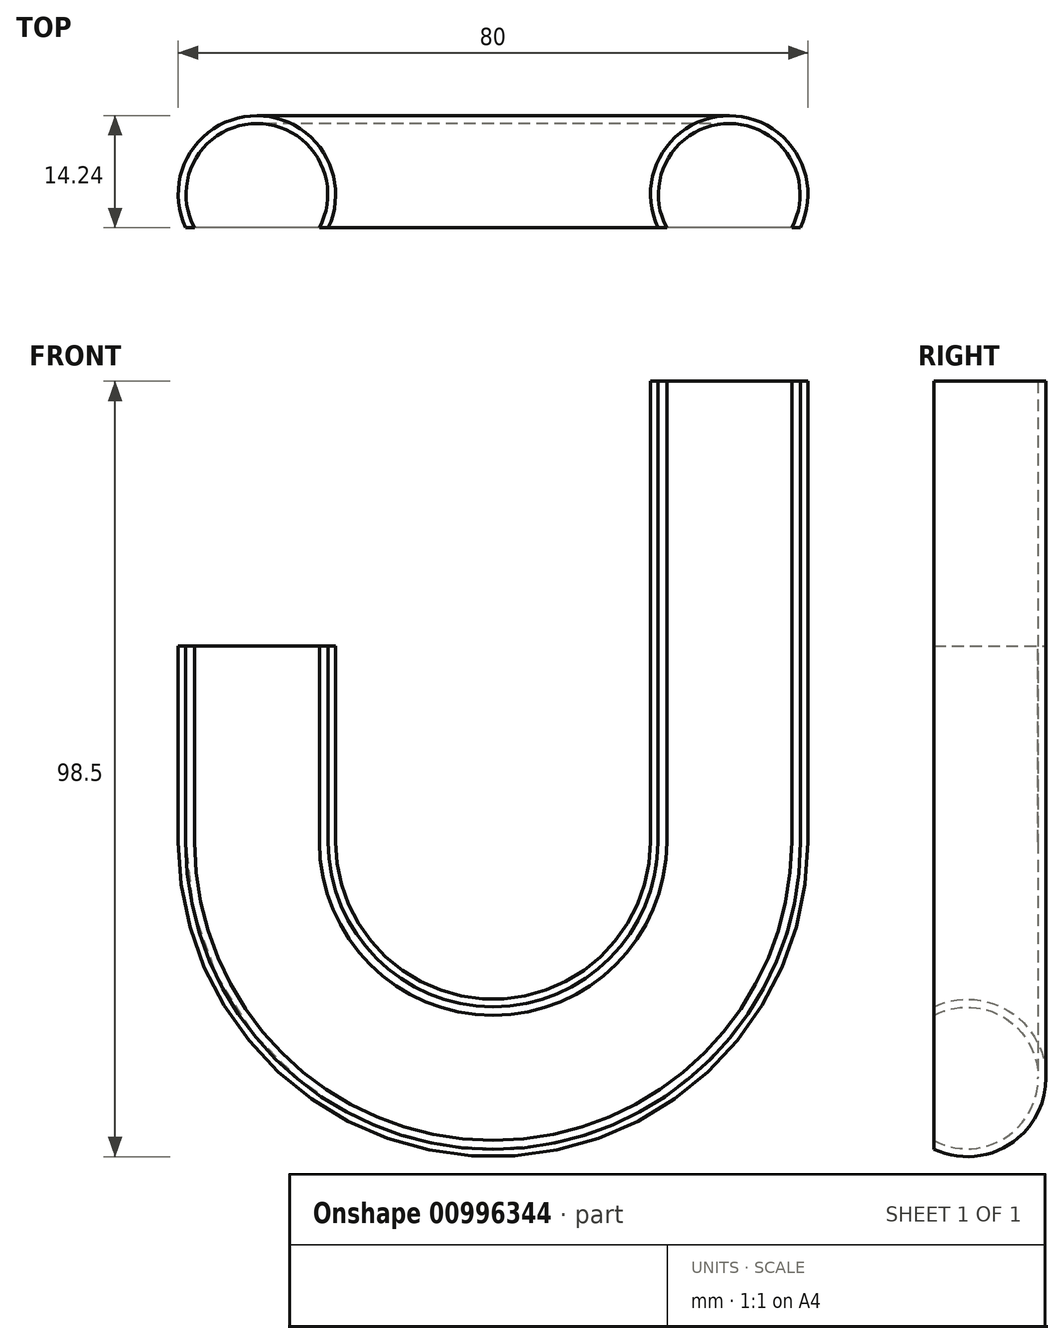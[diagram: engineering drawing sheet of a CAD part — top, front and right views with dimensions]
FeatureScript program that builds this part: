
annotation { "Feature Type Name" : "Feature", "Feature Type Description" : "" }
export const myFeature = defineFeature(function(context is Context, id is Id, definition is map)
    precondition{}
    {
        {
            var Q0;
            Q0=qCreatedBy(makeId("Front.planeOp"),FACE);
            var sketch = newSketch(context, id + "F0", { "sketchPlane" : qUnion([Q0])});
            skLineSegment(sketch, "E0", {"start": v(-30, 24.9) * mm, "end": v(-30, 0) * mm});
            skLineSegment(sketch, "E1", {"start": v(30, 58.5) * mm, "end": v(30, 0) * mm});
            skArc(sketch, "E2", {"start": v(-30, 0) * mm, "mid": v(0, -30) * mm, "end": v(30, 0) * mm});
            skSolve(sketch);
        }
        {
            var Q0;
            Q0=sQuery(id+"F0.wireOp",VERTEX,"E1.start");
            var Q1;
            Q1=sQuery(id+"F0.wireOp",EDGE,"E1");
            cPlane(context, id + "F1", {"entities" : qUnion([Q0, Q1]), "cplaneType" : CPlaneType.CURVE_POINT, "offset" : 25 * mm, "width" : 150 * mm, "height" : 150 * mm});
        }
        {
            var Q0;
            Q0=qCreatedBy(id+"F1.planeOp",FACE);
            var sketch = newSketch(context, id + "F2", { "sketchPlane" : qUnion([Q0])});
            skCircle(sketch, "E3", {"center": v(30, 0) * mm, "radius": 10 * mm});
            skSolve(sketch);
        }
        {
            var Q0;
            Q0=makeQuery(id+"F2.imprint","IMPRINT",FACE,{"disambiguationData":[TD([[makeQuery(id+"F2.imprint","IMPRINT",EDGE,{"derivedFrom":sQuery(id+"F2.wireOp",EDGE,"E3")}),1.0]])]});
            var Q1;
            Q1=sQuery(id+"F0.wireOp",EDGE,"E1");
            var Q2;
            Q2=sQuery(id+"F0.wireOp",EDGE,"E2");
            var Q3;
            Q3=sQuery(id+"F0.wireOp",EDGE,"E0");
            sweep(context, id + "F3", {"profiles" : qUnion([Q0]), "path" : qUnion([Q1, Q2, Q3])});
        }
        {
            var Q0;
            Q0=makeQuery(id+"F3.opSweep","CAP_FACE",FACE,{"disambiguationData":[OSD([sQuery(id+"F0.wireOp",VERTEX,"E1.start"),sQuery(id+"F2.wireOp",EDGE,"E3")])],"isStart":true});
            var sketch = newSketch(context, id + "F4", { "sketchPlane" : qUnion([Q0])});
            skCircle(sketch, "E4", {"center": v(30, 0) * mm, "radius": 9 * mm});
            skSolve(sketch);
        }
        {
            var Q0;
            Q0=makeQuery(id+"F4.imprint","IMPRINT",FACE,{"disambiguationData":[TD([[makeQuery(id+"F4.imprint","IMPRINT",EDGE,{"derivedFrom":sQuery(id+"F4.wireOp",EDGE,"E4")}),1.0]])]});
            var Q1;
            Q1 = qConstructionFilter(qBodyType(qCreatedBy(id + "F0" ,EDGE), BodyType.WIRE), ConstructionObject.NO);
            sweep(context, id + "F5", {"operationType" : NewBodyOperationType.REMOVE, "profiles" : qUnion([Q0]), "path" : qUnion([Q1])});
        }
        {
            var Q0;
            Q0=qCreatedBy(makeId("Top.planeOp"),FACE);
            var sketch = newSketch(context, id + "F6", { "sketchPlane" : qUnion([Q0])});
            skLineSegment(sketch, "E5.bottom", {"start": v(-44.23, -14.32) * mm, "end": v(41, -14.32) * mm});
            skLineSegment(sketch, "E5.top", {"start": v(-44.23, -4.24) * mm, "end": v(41, -4.24) * mm});
            skLineSegment(sketch, "E5.left", {"start": v(-44.23, -14.32) * mm, "end": v(-44.23, -4.24) * mm});
            skLineSegment(sketch, "E5.right", {"start": v(41, -14.32) * mm, "end": v(41, -4.24) * mm});
            skSolve(sketch);
        }
        {
            var Q0;
            Q0=makeQuery(id+"F6.imprint","IMPRINT",FACE,{"disambiguationData":[TD([[makeQuery(id+"F6.imprint","IMPRINT",EDGE,{"derivedFrom":sQuery(id+"F6.wireOp",EDGE,"E5.bottom")}),1.0]])]});
            extrude(context, id + "F7", {"entities" : qUnion([Q0]), "endBound" : BoundingType.SYMMETRIC, "depth" : 120 * mm, "offsetDistance" : 25 * mm});
        }
        {
            var Q0;
            Q0=makeQuery(id+"F7.opExtrude","SWEPT_BODY",BODY,{"disambiguationData":[OSD([sQuery(id+"F6.wireOp",EDGE,"E5.bottom"),sQuery(id+"F6.wireOp",EDGE,"E5.top"),sQuery(id+"F6.wireOp",EDGE,"E5.left"),sQuery(id+"F6.wireOp",EDGE,"E5.right")])]});
            var Q1;
            Q1=makeQuery(id+"F3.opSweep","SWEPT_BODY",BODY,{"disambiguationData":[OSD([sQuery(id+"F0.wireOp",EDGE,"E0"),sQuery(id+"F2.wireOp",EDGE,"E3")])]});
            booleanBodies(context, id + "F8", {"operationType" : BooleanOperationType.SUBTRACTION, "tools" : qUnion([Q0]), "targets" : qUnion([Q1])});
        }
    });
